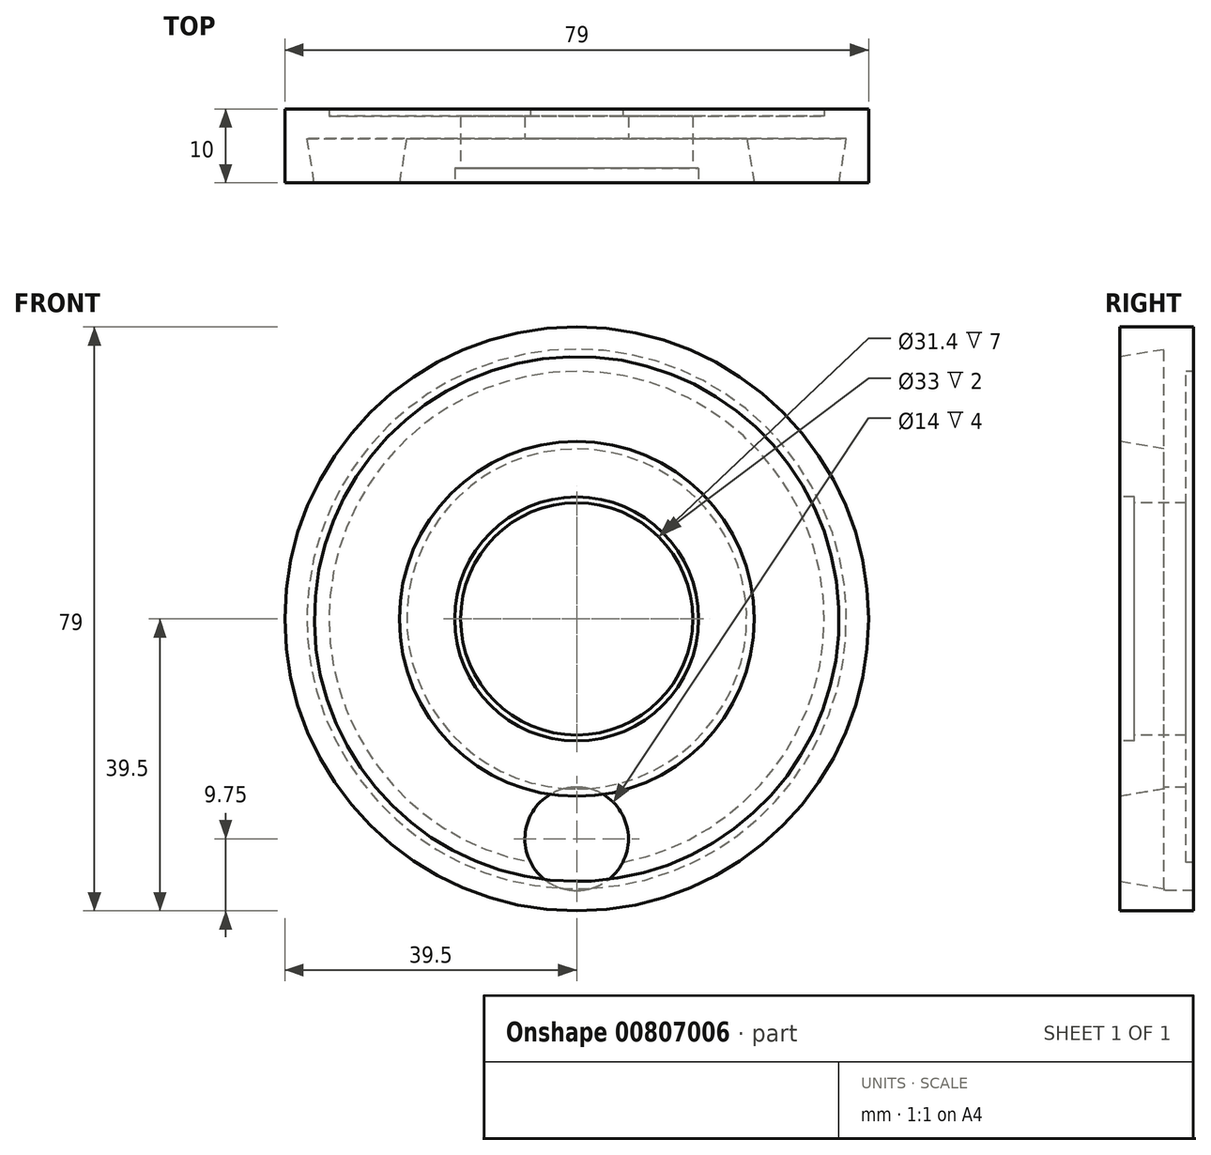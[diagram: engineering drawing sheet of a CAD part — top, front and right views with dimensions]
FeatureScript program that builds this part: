
annotation { "Feature Type Name" : "Feature", "Feature Type Description" : "" }
export const myFeature = defineFeature(function(context is Context, id is Id, definition is map)
    precondition{}
    {
        {
            var Q0;
            Q0=qCreatedBy(makeId("Right.planeOp"),FACE);
            var sketch = newSketch(context, id + "F0", { "sketchPlane" : qUnion([Q0])});
            skLineSegment(sketch, "E0", {"start": v(-59.06, 16.5) * mm, "end": v(-59.06, 24) * mm});
            skLineSegment(sketch, "E1", {"start": v(-59.06, 24) * mm, "end": v(-53.06, 23) * mm});
            skLineSegment(sketch, "E2", {"start": v(-53.06, 23) * mm, "end": v(-53.06, 36.5) * mm});
            skLineSegment(sketch, "E3", {"start": v(-53.06, 36.5) * mm, "end": v(-59.06, 35.5) * mm});
            skLineSegment(sketch, "E4", {"start": v(-59.06, 35.5) * mm, "end": v(-59.06, 39.5) * mm});
            skLineSegment(sketch, "E5", {"start": v(-59.06, 39.5) * mm, "end": v(-49.06, 39.5) * mm});
            skPoint(sketch, "E6.orphan", {"position": v(-176.87, 0) * mm});
            skLineSegment(sketch, "E7", {"start": v(-49.06, 39.5) * mm, "end": v(-49.06, 33.5) * mm});
            skLineSegment(sketch, "E8", {"start": v(-49.06, 33.5) * mm, "end": v(-50.06, 33.5) * mm});
            skLineSegment(sketch, "E9", {"start": v(-59.06, 24) * mm, "end": v(-62.65, 24) * mm, "construction": true});
            skLineSegment(sketch, "E10", {"start": v(-59.06, 35.5) * mm, "end": v(-59.06, 24) * mm, "construction": true});
            skLineSegment(sketch, "E11", {"start": v(-62.65, 24) * mm, "end": v(-62.65, 0) * mm, "construction": true});
            skLineSegment(sketch, "E12", {"start": v(-50.06, 15.7) * mm, "end": v(-57.06, 15.7) * mm});
            skLineSegment(sketch, "E13", {"start": v(-57.06, 15.7) * mm, "end": v(-57.06, 16.5) * mm});
            skLineSegment(sketch, "E14", {"start": v(-57.06, 16.5) * mm, "end": v(-59.06, 16.5) * mm});
            skPoint(sketch, "E15.orphan", {"position": v(171.59, 0) * mm});
            skPoint(sketch, "E16.start.orphan", {"position": v(0, 101.82) * mm});
            skLineSegment(sketch, "E17", {"start": v(-59.06, 29.75) * mm, "end": v(-53.06, 29.75) * mm, "construction": true});
            skLineSegment(sketch, "E18", {"start": v(-50.06, 33.5) * mm, "end": v(-50.06, 15.7) * mm});
            skLineSegment(sketch, "E19", {"start": v(-87.64, 0) * mm, "end": v(0, 0) * mm});
            skLineSegment(sketch, "E20", {"start": v(-50.06, 15.7) * mm, "end": v(-50.06, 0) * mm, "construction": true});
            skLineSegment(sketch, "E21", {"start": v(-51.85, 39.5) * mm, "end": v(-51.85, 0) * mm, "construction": true});
            skLineSegment(sketch, "E22", {"start": v(-49.06, 33.5) * mm, "end": v(-49.06, 0) * mm, "construction": true});
            skLineSegment(sketch, "E23", {"start": v(-59.06, 16.5) * mm, "end": v(-59.06, 0) * mm, "construction": true});
            skSolve(sketch);
        }
        {
            var Q0;
            {var subQ5=sQuery(id+"F0.wireOp",EDGE,"E0");Q0=makeQuery(id+"F0.imprint","IMPRINT",FACE,{"disambiguationData":[TD([[makeQuery(id+"F0.imprint","IMPRINT",EDGE,{"derivedFrom":subQ5}),-1.0]])]});}
            var Q1;
            {var subQ5=sQuery(id+"F0.wireOp",EDGE,"DVSM1hyc-2Y6S-zE7S-hNkl-QA37CpquHjl7");Q1=makeQuery(id+"F0.imprint","IMPRINT",FACE,{"disambiguationData":[TD([[makeQuery(id+"F0.imprint","IMPRINT",EDGE,{"derivedFrom":subQ5}),-1.0]])]});}
            var Q2;
            Q2=sQuery(id+"F0.wireOp",EDGE,"E19");
            revolve(context, id + "F1", {"surfaceOperationType" : NewSurfaceOperationType.NEW, "entities" : qUnion([Q0, Q1]), "axis" : qUnion([Q2]), "revolveType" : RevolveType.FULL});
        }
        {
            var Q0;
            Q0=makeQuery(id+"F1.opRevolve","SWEPT_FACE",FACE,{"disambiguationData":[OSD([sQuery(id+"F0.wireOp",EDGE,"E2")])]});
            var sketch = newSketch(context, id + "F2", { "sketchPlane" : qUnion([Q0])});
            skCircle(sketch, "E24", {"center": v(0, -29.75) * mm, "radius": 7 * mm});
            skPoint(sketch, "E25.orphan", {"position": v(0, -36.5) * mm});
            skPoint(sketch, "E26.end.orphan", {"position": v(0, -23) * mm});
            skSolve(sketch);
        }
        {
            var Q0;
            Q0=qSketchRegion(id+"F2",true);
            var Q1;
            {var subQ0=sQuery(id+"F2.wireOp",EDGE,"E24");var subQ1=sQuery(id+"F0.wireOp",EDGE,"E2");var subQ2=makeQuery(id+"F1.opRevolve","SWEPT_EDGE",EDGE,{"disambiguationData":[OSD([subQ1,sQuery(id+"F0.wireOp",EDGE,"E3")])]});var subQ3=makeQuery(id+"F2.imprint","INTERSECT",VERTEX,{"disambiguationData":[OD(0.0)],"derivedFrom":[subQ2,subQ0]});Q1=makeQuery(id+"F2.imprint","IMPRINT",FACE,{"disambiguationData":[TD([[makeQuery(id+"F2.imprint","IMPRINT",EDGE,{"disambiguationData":[TD([[subQ3,-1.0]])],"derivedFrom":subQ0}),1.0]])]});}
            extrude(context, id + "F3", {"entities" : qUnion([Q0, Q1]), "operationType" : NewBodyOperationType.REMOVE, "endBound" : BoundingType.THROUGH_ALL, "oppositeDirection" : true, "depth" : 4 * mm, "offsetDistance" : 25 * mm});
        }
        {
            var Q0;
            Q0=makeQuery(id+"F1.opRevolve","SWEPT_FACE",FACE,{"disambiguationData":[OSD([sQuery(id+"F0.wireOp",EDGE,"E0")])]});
            var sketch = newSketch(context, id + "F4", { "sketchPlane" : qUnion([Q0])});
            skLineSegment(sketch, "E27", {"start": v(0, 52.66) * mm, "end": v(0, -63.94) * mm, "construction": true});
            skLineSegment(sketch, "E28", {"start": v(-58.62, 0) * mm, "end": v(67.13, 0) * mm, "construction": true});
            skSolve(sketch);
        }
    });
